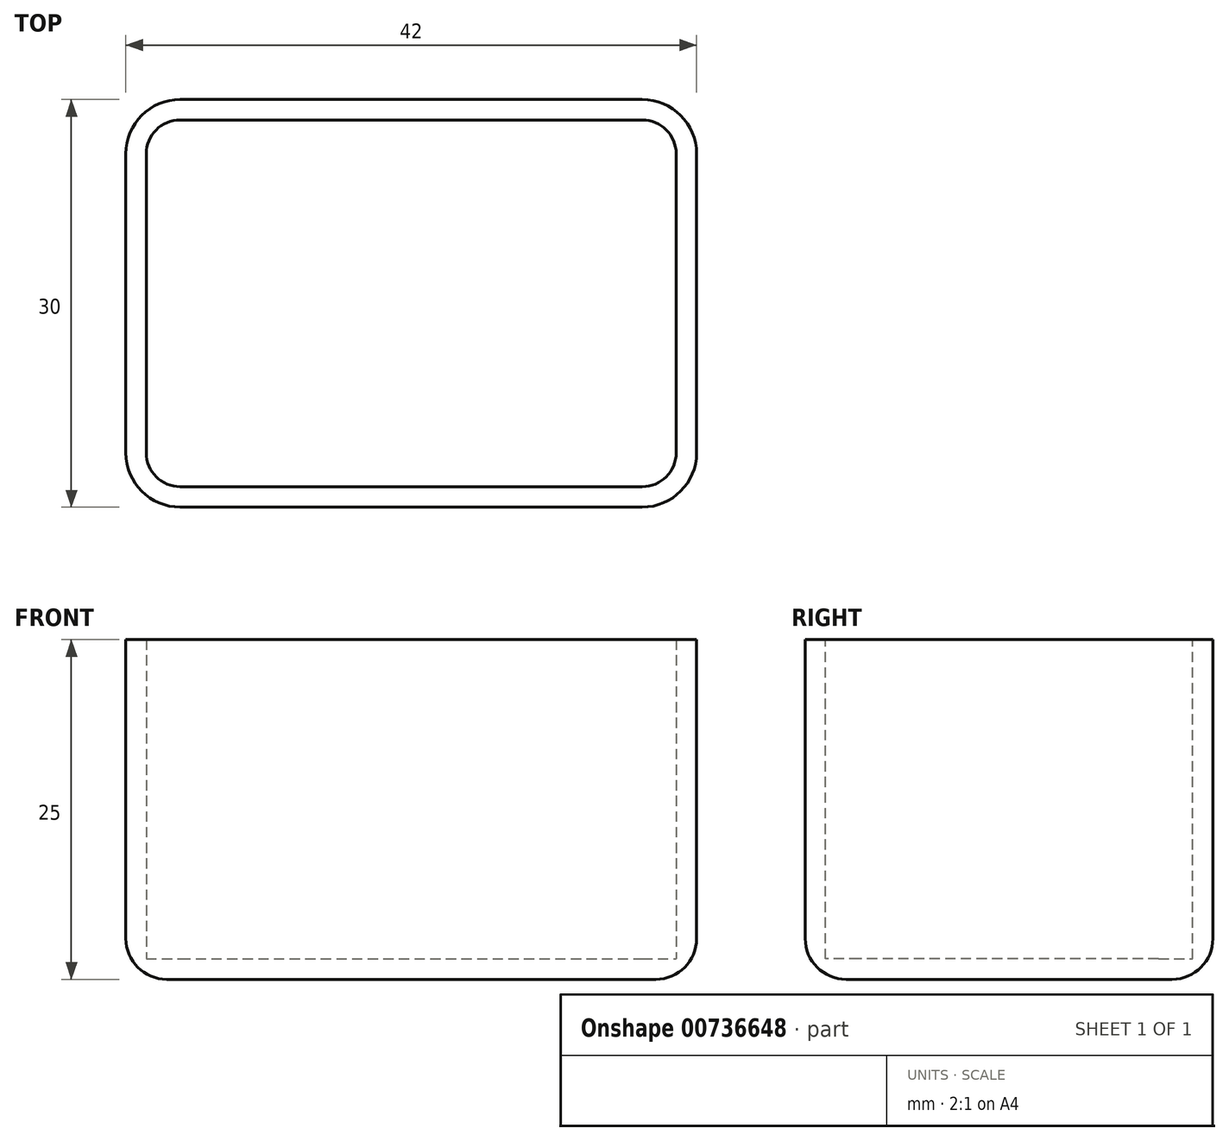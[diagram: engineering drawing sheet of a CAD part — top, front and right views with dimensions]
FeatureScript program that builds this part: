
annotation { "Feature Type Name" : "Feature", "Feature Type Description" : "" }
export const myFeature = defineFeature(function(context is Context, id is Id, definition is map)
    precondition{}
    {
        {
            var Q0;
            Q0=qCreatedBy(makeId("Top.planeOp"),FACE);
            var sketch = newSketch(context, id + "F0", { "sketchPlane" : qUnion([Q0]), "asVersion" : FeatureScriptVersionNumber.V608_MERGE_FROM_TOOLS});
            skLineSegment(sketch, "E0.bottom", {"start": v(-6.54, 18.07) * mm, "end": v(27.46, 18.07) * mm});
            skLineSegment(sketch, "E0.top", {"start": v(-6.54, -11.93) * mm, "end": v(27.46, -11.93) * mm});
            skLineSegment(sketch, "E0.left", {"start": v(-10.54, 14.07) * mm, "end": v(-10.54, -7.93) * mm});
            skLineSegment(sketch, "E0.right", {"start": v(31.46, 14.07) * mm, "end": v(31.46, -7.93) * mm});
            skPoint(sketch, "E1.visualSharp", {"position": v(-10.54, 18.07) * mm});
            skArc(sketch, "E1.filletArc", {"start": v(-6.54, 18.07) * mm, "mid": v(-9.37, 16.9) * mm, "end": v(-10.54, 14.07) * mm});
            skPoint(sketch, "E2.visualSharp", {"position": v(-10.54, -11.93) * mm});
            skArc(sketch, "E2.filletArc", {"start": v(-10.54, -7.93) * mm, "mid": v(-9.37, -10.76) * mm, "end": v(-6.54, -11.93) * mm});
            skPoint(sketch, "E3.visualSharp", {"position": v(31.46, 18.07) * mm});
            skArc(sketch, "E3.filletArc", {"start": v(31.46, 14.07) * mm, "mid": v(30.3, 16.9) * mm, "end": v(27.46, 18.07) * mm});
            skPoint(sketch, "E4.visualSharp", {"position": v(31.46, -11.93) * mm});
            skArc(sketch, "E4.filletArc", {"start": v(27.46, -11.93) * mm, "mid": v(30.3, -10.76) * mm, "end": v(31.46, -7.93) * mm});
            skSolve(sketch);
        }
        {
            var Q0;
            Q0=makeQuery(id+"F0.imprint","IMPRINT",FACE,{"disambiguationData":[TD([[makeQuery(id+"F0.imprint","IMPRINT",EDGE,{"derivedFrom":sQuery(id+"F0.wireOp",EDGE,"E0.bottom")}),-1.0]])]});
            extrude(context, id + "F1", {"entities" : qUnion([Q0]), "depth" : 25 * mm, "offsetDistance" : 25 * mm});
        }
        {
            var Q0;
            Q0=makeQuery(id+"F1.opExtrude","CAP_FACE",FACE,{"disambiguationData":[OSD([sQuery(id+"F0.wireOp",EDGE,"E0.bottom"),sQuery(id+"F0.wireOp",EDGE,"E0.top"),sQuery(id+"F0.wireOp",EDGE,"E0.left"),sQuery(id+"F0.wireOp",EDGE,"E0.right"),sQuery(id+"F0.wireOp",EDGE,"E1.filletArc"),sQuery(id+"F0.wireOp",EDGE,"E2.filletArc"),sQuery(id+"F0.wireOp",EDGE,"E3.filletArc"),sQuery(id+"F0.wireOp",EDGE,"E4.filletArc")])],"isStart":false});
            shell(context, id + "F2", {"entities" : qUnion([Q0]), "thickness" : 1.5 * mm});
        }
        {
            var Q0;
            Q0=makeQuery(id+"F1.opExtrude","CAP_EDGE",EDGE,{"disambiguationData":[OSD([sQuery(id+"F0.wireOp",EDGE,"E0.top")])],"isStart":true});
            fillet(context, id + "F3", {"entities" : qUnion([Q0]), "radius" : 3 * mm, "tangentPropagation" : true, "allowEdgeOverflow" : false});
        }
    });
